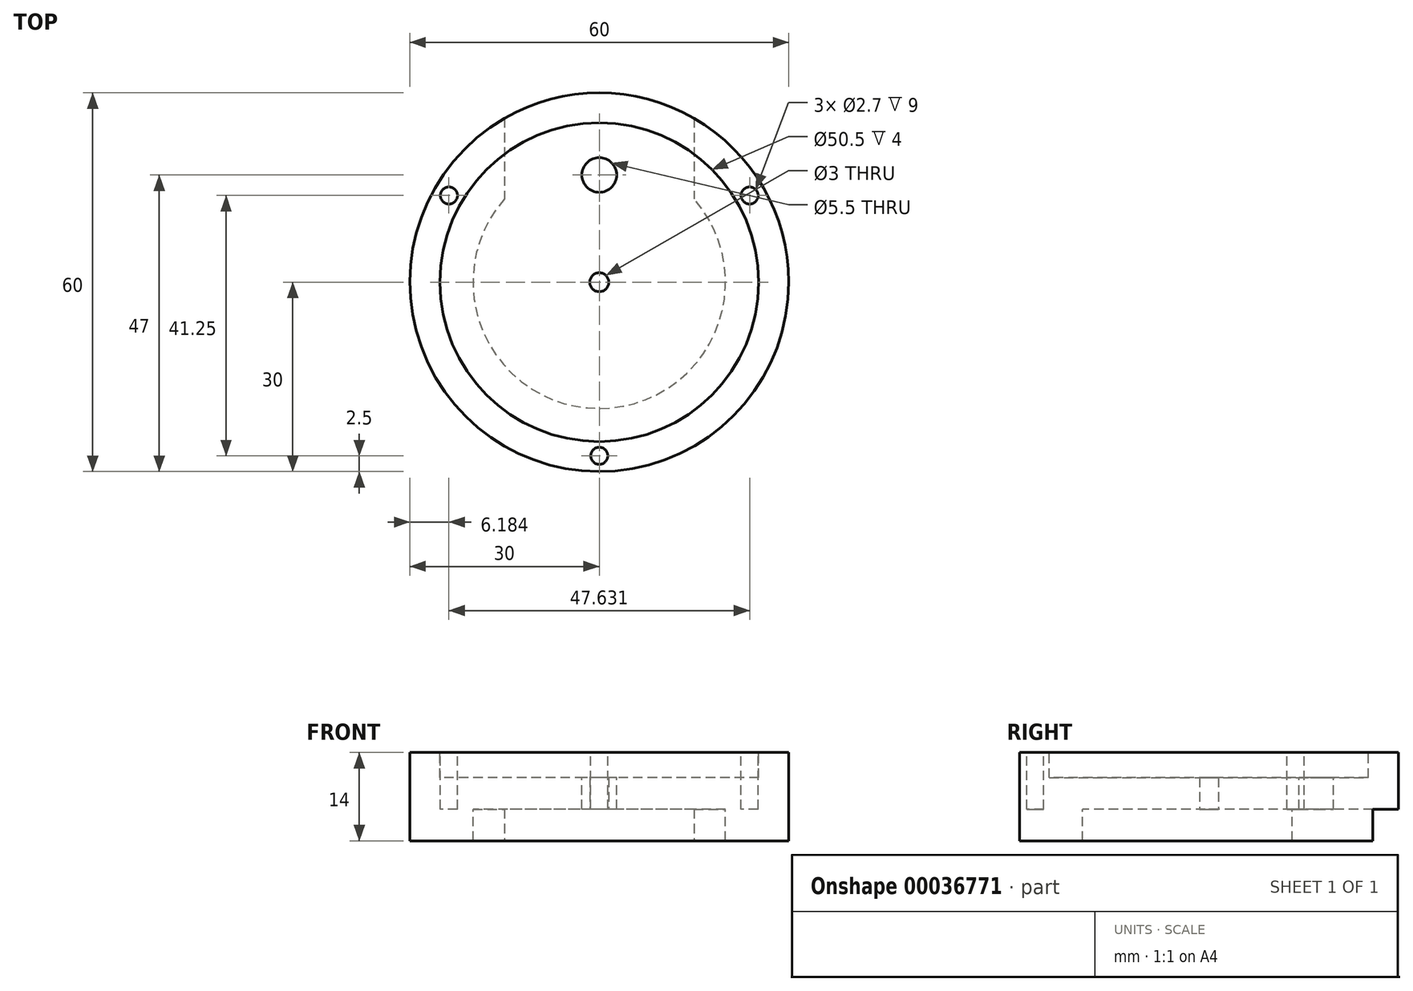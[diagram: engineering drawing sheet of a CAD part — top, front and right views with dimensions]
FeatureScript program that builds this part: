
annotation { "Feature Type Name" : "Feature", "Feature Type Description" : "" }
export const myFeature = defineFeature(function(context is Context, id is Id, definition is map)
    precondition{}
    {
        {
            var Q0;
            Q0=qCreatedBy(makeId("Top.planeOp"),FACE);
            var sketch = newSketch(context, id + "F0", { "sketchPlane" : qUnion([Q0])});
            skCircle(sketch, "E0", {"center": v(0, 0) * mm, "radius": 30 * mm});
            skSolve(sketch);
        }
        {
            var Q0;
            Q0=makeQuery(id+"F0.imprint","IMPRINT",FACE,{"disambiguationData":[TD([[makeQuery(id+"F0.imprint","IMPRINT",EDGE,{"derivedFrom":sQuery(id+"F0.wireOp",EDGE,"E0")}),1.0]])]});
            extrude(context, id + "F1", {"entities" : qUnion([Q0]), "depth" : 9 * mm});
        }
        {
            var Q0;
            Q0=makeQuery(id+"F1.opExtrude","CAP_FACE",FACE,{"disambiguationData":[OSD([sQuery(id+"F0.wireOp",EDGE,"E0")])],"isStart":false});
            var sketch = newSketch(context, id + "F2", { "sketchPlane" : qUnion([Q0])});
            skCircle(sketch, "E1", {"center": v(0, 0) * mm, "radius": 25.25 * mm});
            skSolve(sketch);
        }
        {
            var Q0;
            Q0=makeQuery(id+"F2.imprint","IMPRINT",FACE,{"disambiguationData":[TD([[makeQuery(id+"F2.imprint","IMPRINT",EDGE,{"derivedFrom":sQuery(id+"F2.wireOp",EDGE,"E1")}),1.0]])]});
            extrude(context, id + "F3", {"entities" : qUnion([Q0]), "operationType" : NewBodyOperationType.REMOVE, "oppositeDirection" : true, "depth" : 4 * mm});
        }
        {
            var Q0;
            Q0=qCreatedBy(makeId("Top.planeOp"),FACE);
            var sketch = newSketch(context, id + "F4", { "sketchPlane" : qUnion([Q0])});
            skCircle(sketch, "E2", {"center": v(0, 0) * mm, "radius": 1.5 * mm});
            skSolve(sketch);
        }
        {
            var Q0;
            Q0=makeQuery(id+"F4.imprint","IMPRINT",FACE,{"disambiguationData":[TD([[makeQuery(id+"F4.imprint","IMPRINT",EDGE,{"derivedFrom":sQuery(id+"F4.wireOp",EDGE,"E2")}),1.0]])]});
            var Q1;
            Q1=sQuery(id+"F4.wireOp",EDGE,"E2");
            extrude(context, id + "F5", {"entities" : qUnion([Q0]), "operationType" : NewBodyOperationType.REMOVE, "surfaceEntities" : qUnion([Q1]), "endBound" : BoundingType.THROUGH_ALL, "depth" : 25 * mm});
        }
        {
            var Q0;
            Q0=makeQuery(id+"F1.opExtrude","CAP_FACE",FACE,{"disambiguationData":[OSD([sQuery(id+"F0.wireOp",EDGE,"E0")])],"isStart":false});
            var sketch = newSketch(context, id + "F6", { "sketchPlane" : qUnion([Q0])});
            skLineSegment(sketch, "E3", {"start": v(0, 0) * mm, "end": v(25.25, 0) * mm, "construction": true});
            skCircle(sketch, "E4", {"center": v(23.82, 13.75) * mm, "radius": 1.35 * mm});
            skCircle(sketch, "E5", {"center": v(0, -27.5) * mm, "radius": 1.35 * mm});
            skLineSegment(sketch, "E6", {"start": v(0, 0) * mm, "end": v(23.82, 13.75) * mm, "construction": true});
            skLineSegment(sketch, "E7", {"start": v(0, 0) * mm, "end": v(0, -27.5) * mm, "construction": true});
            skLineSegment(sketch, "E8", {"start": v(0, 0) * mm, "end": v(-23.82, 13.75) * mm, "construction": true});
            skCircle(sketch, "E9", {"center": v(-23.82, 13.75) * mm, "radius": 1.35 * mm});
            skSolve(sketch);
        }
        {
            var Q0;
            Q0=makeQuery(id+"F6.imprint","IMPRINT",FACE,{"disambiguationData":[TD([[makeQuery(id+"F6.imprint","IMPRINT",EDGE,{"derivedFrom":sQuery(id+"F6.wireOp",EDGE,"E4")}),1.0]])]});
            var Q1;
            Q1=makeQuery(id+"F6.imprint","IMPRINT",FACE,{"disambiguationData":[TD([[makeQuery(id+"F6.imprint","IMPRINT",EDGE,{"derivedFrom":sQuery(id+"F6.wireOp",EDGE,"E5")}),1.0]])]});
            var Q2;
            Q2=makeQuery(id+"F6.imprint","IMPRINT",FACE,{"disambiguationData":[TD([[makeQuery(id+"F6.imprint","IMPRINT",EDGE,{"derivedFrom":sQuery(id+"F6.wireOp",EDGE,"E9")}),1.0]])]});
            var Q3;
            Q3=sQuery(id+"F6.wireOp",EDGE,"ec20421c-758a-4dcc-8e2b-3ec363aacf1b");
            var Q4;
            Q4=sQuery(id+"F6.wireOp",EDGE,"3d322e7b-1bf5-4eee-8f98-b2096053c3f1");
            extrude(context, id + "F7", {"entities" : qUnion([Q0, Q1, Q2]), "operationType" : NewBodyOperationType.REMOVE, "surfaceEntities" : qUnion([Q3, Q4]), "endBound" : BoundingType.THROUGH_ALL, "oppositeDirection" : true, "depth" : 25 * mm});
        }
        {
            var Q0;
            Q0=makeQuery(id+"F3.boolean.opBoolean","COPY",FACE,{"derivedFrom":makeQuery(id+"F3.opExtrude","CAP_FACE",FACE,{"disambiguationData":[OSD([sQuery(id+"F2.wireOp",EDGE,"E1")])],"isStart":false})});
            var sketch = newSketch(context, id + "F8", { "sketchPlane" : qUnion([Q0])});
            skLineSegment(sketch, "E10", {"start": v(0, 0) * mm, "end": v(0, 17) * mm, "construction": true});
            skCircle(sketch, "E11", {"center": v(0, 17) * mm, "radius": 2.75 * mm});
            skSolve(sketch);
        }
        {
            var Q0;
            Q0=makeQuery(id+"F8.imprint","IMPRINT",FACE,{"disambiguationData":[TD([[makeQuery(id+"F8.imprint","IMPRINT",EDGE,{"derivedFrom":sQuery(id+"F8.wireOp",EDGE,"E11")}),1.0]])]});
            var Q1;
            Q1=sQuery(id+"F8.wireOp",EDGE,"E11");
            extrude(context, id + "F9", {"entities" : qUnion([Q0]), "operationType" : NewBodyOperationType.REMOVE, "surfaceEntities" : qUnion([Q1]), "endBound" : BoundingType.THROUGH_ALL, "oppositeDirection" : true, "depth" : 25 * mm});
        }
        {
            var Q0;
            Q0=makeQuery(id+"F1.opExtrude","CAP_FACE",FACE,{"disambiguationData":[OSD([sQuery(id+"F0.wireOp",EDGE,"E0")])],"isStart":true});
            var sketch = newSketch(context, id + "F10", { "sketchPlane" : qUnion([Q0])});
            skCircle(sketch, "E12", {"center": v(0, 0) * mm, "radius": 30 * mm});
            skCircle(sketch, "E13", {"center": v(0, 0) * mm, "radius": 20 * mm});
            skSolve(sketch);
        }
        {
            var Q0;
            Q0 = qSketchRegion(id + "F10", true);
            extrude(context, id + "F11", {"entities" : qUnion([Q0]), "operationType" : NewBodyOperationType.ADD, "depth" : 5 * mm});
        }
        {
            var Q0;
            Q0=qCreatedBy(makeId("Top.planeOp"),FACE);
            var sketch = newSketch(context, id + "F12", { "sketchPlane" : qUnion([Q0])});
            skLineSegment(sketch, "E14.rect.bottom", {"start": v(-15, 33.3) * mm, "end": v(15, 33.3) * mm});
            skLineSegment(sketch, "E14.rect.top", {"start": v(-15, 8.53) * mm, "end": v(15, 8.53) * mm});
            skLineSegment(sketch, "E14.rect.left", {"start": v(-15, 33.3) * mm, "end": v(-15, 8.53) * mm});
            skLineSegment(sketch, "E14.rect.right", {"start": v(15, 33.3) * mm, "end": v(15, 8.53) * mm});
            skPoint(sketch, "E14.rect.middle", {"position": v(0, 20.91) * mm});
            skSolve(sketch);
        }
        {
            var Q0;
            Q0=makeQuery(id+"F12.imprint","IMPRINT",FACE,{"disambiguationData":[TD([[makeQuery(id+"F12.imprint","IMPRINT",EDGE,{"derivedFrom":sQuery(id+"F12.wireOp",EDGE,"E14.rect.bottom")}),-1.0]])]});
            extrude(context, id + "F13", {"entities" : qUnion([Q0]), "operationType" : NewBodyOperationType.REMOVE, "oppositeDirection" : true, "depth" : 5 * mm});
        }
    });
